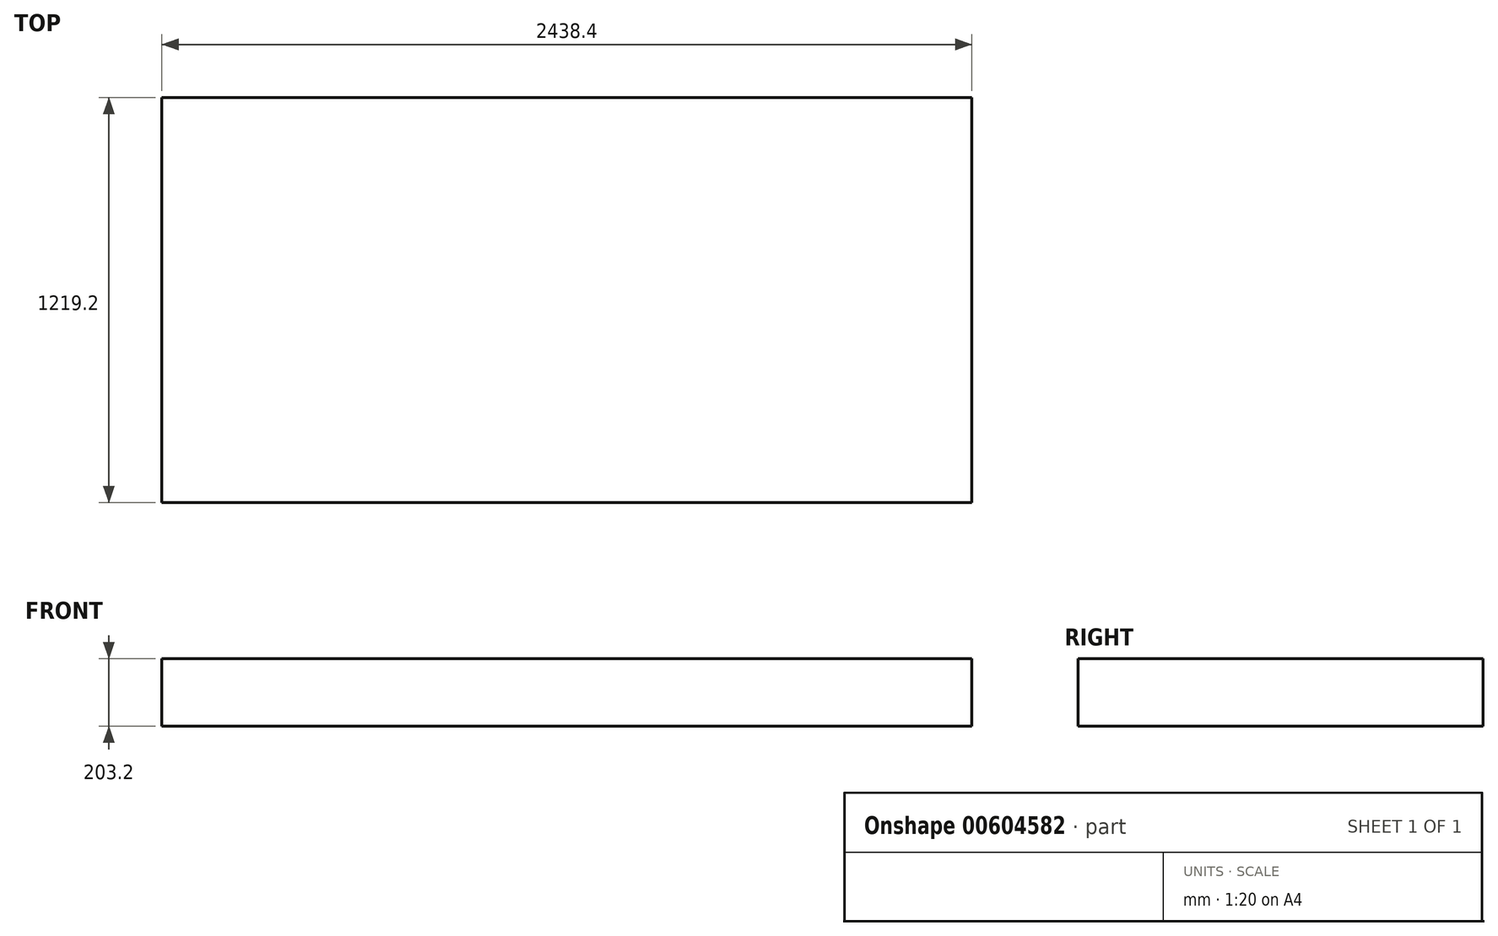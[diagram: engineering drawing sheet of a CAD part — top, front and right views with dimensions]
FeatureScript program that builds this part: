
annotation { "Feature Type Name" : "Feature", "Feature Type Description" : "" }
export const myFeature = defineFeature(function(context is Context, id is Id, definition is map)
    precondition{}
    {
        {
            var Q0;
            Q0=qCreatedBy(makeId("Top.planeOp"),FACE);
            var sketch = newSketch(context, id + "F0", { "sketchPlane" : qUnion([Q0])});
            skLineSegment(sketch, "E0.bottom", {"start": v(1219.2, -609.6) * mm, "end": v(-1219.2, -609.6) * mm});
            skLineSegment(sketch, "E0.top", {"start": v(1219.2, 609.6) * mm, "end": v(-1219.2, 609.6) * mm});
            skLineSegment(sketch, "E0.left", {"start": v(1219.2, -609.6) * mm, "end": v(1219.2, 609.6) * mm});
            skLineSegment(sketch, "E0.right", {"start": v(-1219.2, -609.6) * mm, "end": v(-1219.2, 609.6) * mm});
            skPoint(sketch, "E0.middle", {"position": v(0, 0) * mm});
            skSolve(sketch);
        }
        {
            var Q0;
            Q0=qCreatedBy(makeId("Right.planeOp"),FACE);
            var Q1;
            Q1=sQuery(id+"F0.wireOp",VERTEX,"E0.bottom.start");
            cPlane(context, id + "F1", {"entities" : qUnion([Q0, Q1]), "cplaneType" : CPlaneType.PLANE_POINT, "offset" : 25.4 * mm, "width" : 152.4 * mm, "height" : 152.4 * mm});
        }
        {
            var Q0;
            Q0=qCreatedBy(id+"F1.planeOp",FACE);
            var sketch = newSketch(context, id + "F2", { "sketchPlane" : qUnion([Q0])});
            skLineSegment(sketch, "E1", {"start": v(-609.6, 0) * mm, "end": v(-609.6, -50.8) * mm});
            skLineSegment(sketch, "E2", {"start": v(609.6, 0) * mm, "end": v(609.6, -101.6) * mm});
            skSolve(sketch);
        }
        {
            var Q0;
            Q0=sQuery(id+"F2.wireOp",VERTEX,"E2.end");
            var Q1;
            Q1=sQuery(id+"F2.wireOp",VERTEX,"E1.end");
            var Q2;
            Q2=sQuery(id+"F0.wireOp",VERTEX,"E0.right.start");
            cPlane(context, id + "F3", {"entities" : qUnion([Q0, Q1, Q2]), "cplaneType" : CPlaneType.THREE_POINT, "offset" : 25.4 * mm, "width" : 152.4 * mm, "height" : 152.4 * mm});
        }
        {
            var Q0;
            Q0 = qSketchRegion(id + "F0", true);
            extrude(context, id + "F4", {"entities" : qUnion([Q0]), "oppositeDirection" : true, "depth" : 203.2 * mm, "offsetDistance" : 25.4 * mm});
        }
    });
